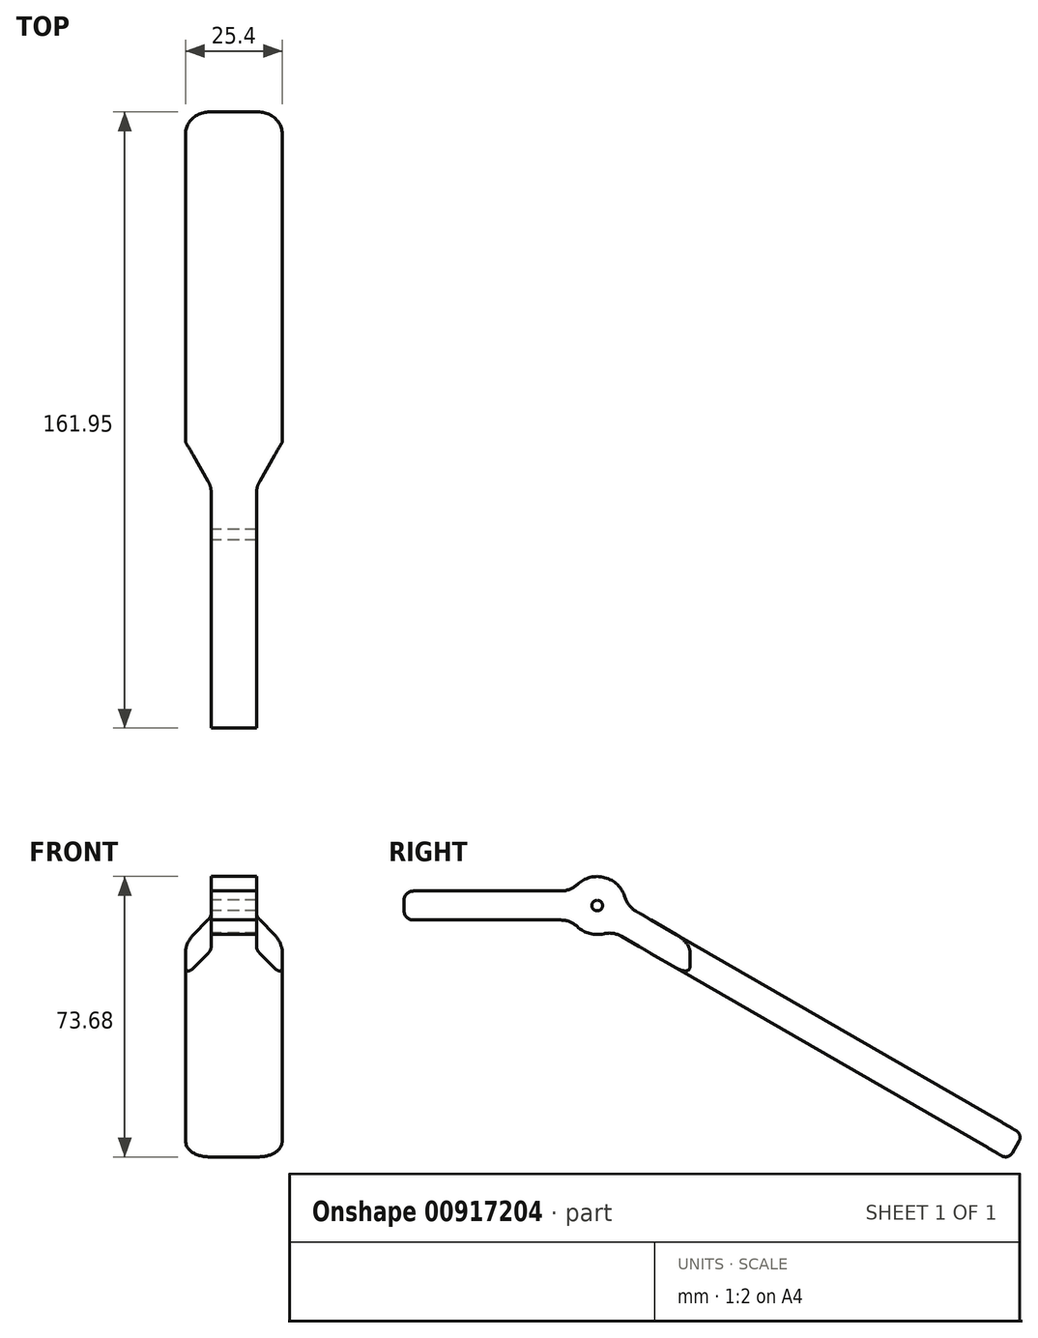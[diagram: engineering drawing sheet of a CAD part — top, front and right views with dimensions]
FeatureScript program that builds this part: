
annotation { "Feature Type Name" : "Feature", "Feature Type Description" : "" }
export const myFeature = defineFeature(function(context is Context, id is Id, definition is map)
    precondition{}
    {
        {
            var Q0;
            Q0=qCreatedBy(makeId("Right.planeOp"),FACE);
            var sketch = newSketch(context, id + "F0", { "sketchPlane" : qUnion([Q0])});
            skCircle(sketch, "E0", {"center": v(0, 0) * mm, "radius": 1.4 * mm});
            skLineSegment(sketch, "E1.bottom", {"start": v(-6.6, -3.81) * mm, "end": v(-50.8, -3.81) * mm});
            skLineSegment(sketch, "E1.top", {"start": v(-6.6, 3.81) * mm, "end": v(-50.8, 3.81) * mm});
            skLineSegment(sketch, "E1.right", {"start": v(-50.8, -3.81) * mm, "end": v(-50.8, 3.81) * mm});
            skPoint(sketch, "E1.middle", {"position": v(-28.7, 0) * mm});
            skLineSegment(sketch, "E2", {"start": v(3.81, -6.6) * mm, "end": v(108.08, -66.8) * mm});
            skLineSegment(sketch, "E3", {"start": v(108.08, -66.8) * mm, "end": v(111.9, -60.2) * mm});
            skLineSegment(sketch, "E4", {"start": v(111.9, -60.2) * mm, "end": v(7.62, 0) * mm});
            skLineSegment(sketch, "E5", {"start": v(0, 0) * mm, "end": v(33.46, -19.32) * mm, "construction": true});
            skLineSegment(sketch, "E6", {"start": v(-152.3, 12.7) * mm, "end": v(68.42, 12.7) * mm, "construction": true});
            skArc(sketch, "E7", {"start": v(-6.6, -3.8) * mm, "mid": v(-1.97, -7.36) * mm, "end": v(3.81, -6.6) * mm});
            skArc(sketch, "E8.trimOffspring", {"start": v(7.62, 0) * mm, "mid": v(1.97, 7.36) * mm, "end": v(-6.6, 3.8) * mm});
            skSolve(sketch);
        }
        {
            var Q0;
            Q0=qSketchRegion(id+"F0",true);
            extrude(context, id + "F1", {"entities" : qUnion([Q0]), "depth" : 25.4 * mm, "offsetDistance" : 25.4 * mm});
        }
        {
            var Q0;
            Q0=qCreatedBy(makeId("Top.planeOp"),FACE);
            cPlane(context, id + "F2", {"entities" : qUnion([Q0]), "cplaneType" : CPlaneType.OFFSET, "offset" : 25.4 * mm, "width" : 152.4 * mm, "height" : 152.4 * mm});
        }
        {
            var Q0;
            Q0=makeQuery(id+"F1.opExtrude","CAP_FACE",FACE,{"disambiguationData":[OSD([sQuery(id+"F0.wireOp",EDGE,"E0"),sQuery(id+"F0.wireOp",EDGE,"w8Ws021I-NBfv-kzaN-iq3K-uN73JVfCB56X"),sQuery(id+"F0.wireOp",EDGE,"E1.bottom"),sQuery(id+"F0.wireOp",EDGE,"E1.top"),sQuery(id+"F0.wireOp",EDGE,"E1.right"),sQuery(id+"F0.wireOp",EDGE,"E2"),sQuery(id+"F0.wireOp",EDGE,"E3"),sQuery(id+"F0.wireOp",EDGE,"E4"),sQuery(id+"F0.wireOp",EDGE,"a2025f1e-f919-408e-afa6-1f2dc75ffb8d.trimOffspring")])],"isStart":false});
            var Q1;
            Q1=makeQuery(id+"F1.opExtrude","CAP_FACE",FACE,{"disambiguationData":[OSD([sQuery(id+"F0.wireOp",EDGE,"E0"),sQuery(id+"F0.wireOp",EDGE,"w8Ws021I-NBfv-kzaN-iq3K-uN73JVfCB56X"),sQuery(id+"F0.wireOp",EDGE,"E1.bottom"),sQuery(id+"F0.wireOp",EDGE,"E1.top"),sQuery(id+"F0.wireOp",EDGE,"E1.right"),sQuery(id+"F0.wireOp",EDGE,"E2"),sQuery(id+"F0.wireOp",EDGE,"E3"),sQuery(id+"F0.wireOp",EDGE,"E4"),sQuery(id+"F0.wireOp",EDGE,"a2025f1e-f919-408e-afa6-1f2dc75ffb8d.trimOffspring")])],"isStart":true});
            cPlane(context, id + "F3", {"entities" : qUnion([Q0, Q1]), "cplaneType" : CPlaneType.MID_PLANE, "offset" : 25.4 * mm, "width" : 152.4 * mm, "height" : 152.4 * mm});
        }
        {
            var Q0;
            Q0=qCreatedBy(id+"F2.planeOp",FACE);
            var sketch = newSketch(context, id + "F4", { "sketchPlane" : qUnion([Q0])});
            skLineSegment(sketch, "E9.right", {"start": v(6.73, 12.7) * mm, "end": v(6.73, -50.8) * mm});
            skLineSegment(sketch, "E10.MirrorCS", {"start": v(18.67, 12.7) * mm, "end": v(18.67, -50.8) * mm});
            skLineSegment(sketch, "E11", {"start": v(6.73, 12.7) * mm, "end": v(0, 24.36) * mm});
            skLineSegment(sketch, "E12", {"start": v(0, 24.36) * mm, "end": v(0, -50.8) * mm});
            skLineSegment(sketch, "E13.MirrorCS", {"start": v(18.67, 12.7) * mm, "end": v(25.4, 24.36) * mm});
            skLineSegment(sketch, "E14.MirrorCS", {"start": v(25.4, 24.36) * mm, "end": v(25.4, -50.8) * mm});
            skLineSegment(sketch, "E15", {"start": v(0, -50.8) * mm, "end": v(6.73, -50.8) * mm});
            skLineSegment(sketch, "E16.MirrorCS", {"start": v(25.4, -50.8) * mm, "end": v(18.67, -50.8) * mm});
            skSolve(sketch);
        }
        {
            var Q0;
            Q0=makeQuery(id+"F4.imprint","IMPRINT",FACE,{"disambiguationData":[TD([[makeQuery(id+"F4.imprint","IMPRINT",EDGE,{"derivedFrom":sQuery(id+"F4.wireOp",EDGE,"E9.right")}),-1.0]])]});
            var Q1;
            Q1=makeQuery(id+"F4.imprint","IMPRINT",FACE,{"disambiguationData":[TD([[makeQuery(id+"F4.imprint","IMPRINT",EDGE,{"derivedFrom":sQuery(id+"F4.wireOp",EDGE,"E10.MirrorCS")}),1.0]])]});
            extrude(context, id + "F5", {"entities" : qUnion([Q0, Q1]), "operationType" : NewBodyOperationType.REMOVE, "endBound" : BoundingType.THROUGH_ALL, "oppositeDirection" : true, "depth" : 25.4 * mm, "offsetDistance" : 25.4 * mm});
        }
        {
            var Q0;
            Q0=makeQuery(id+"F1.opExtrude","SWEPT_EDGE",EDGE,{"disambiguationData":[OSD([sQuery(id+"F0.wireOp",EDGE,"E1.bottom"),sQuery(id+"F0.wireOp",EDGE,"E7")])]});
            var Q1;
            Q1=makeQuery(id+"F1.opExtrude","SWEPT_EDGE",EDGE,{"disambiguationData":[OSD([sQuery(id+"F0.wireOp",EDGE,"E2"),sQuery(id+"F0.wireOp",EDGE,"E7")])]});
            var Q2;
            Q2=makeQuery(id+"F1.opExtrude","SWEPT_EDGE",EDGE,{"disambiguationData":[OSD([sQuery(id+"F0.wireOp",EDGE,"E1.top"),sQuery(id+"F0.wireOp",EDGE,"E8.trimOffspring")])]});
            var Q3;
            Q3=makeQuery(id+"F1.opExtrude","SWEPT_EDGE",EDGE,{"disambiguationData":[OSD([sQuery(id+"F0.wireOp",EDGE,"E4"),sQuery(id+"F0.wireOp",EDGE,"E8.trimOffspring")])]});
            var Q4;
            Q4=makeQuery(id+"F5.boolean.opBoolean","COPY",EDGE,{"derivedFrom":makeQuery(id+"F5.opExtrude","SWEPT_EDGE",EDGE,{"disambiguationData":[OSD([sQuery(id+"F4.wireOp",EDGE,"E10.MirrorCS"),sQuery(id+"F4.wireOp",EDGE,"E13.MirrorCS")])]})});
            var Q5;
            Q5=makeQuery(id+"F5.boolean.opBoolean","COPY",EDGE,{"derivedFrom":makeQuery(id+"F5.opExtrude","SWEPT_EDGE",EDGE,{"disambiguationData":[OSD([sQuery(id+"F4.wireOp",EDGE,"E13.MirrorCS"),sQuery(id+"F4.wireOp",EDGE,"E14.MirrorCS")])]})});
            var Q6;
            Q6=makeQuery(id+"F5.boolean.opBoolean","COPY",EDGE,{"derivedFrom":makeQuery(id+"F5.opExtrude","SWEPT_EDGE",EDGE,{"disambiguationData":[OSD([sQuery(id+"F4.wireOp",EDGE,"E9.right"),sQuery(id+"F4.wireOp",EDGE,"E11")])]})});
            var Q7;
            Q7=makeQuery(id+"F5.boolean.opBoolean","COPY",EDGE,{"derivedFrom":makeQuery(id+"F5.opExtrude","SWEPT_EDGE",EDGE,{"disambiguationData":[OSD([sQuery(id+"F4.wireOp",EDGE,"E11"),sQuery(id+"F4.wireOp",EDGE,"E12")])]})});
            var Q8;
            Q8=makeQuery(id+"F1.opExtrude","CAP_EDGE",EDGE,{"disambiguationData":[OSD([sQuery(id+"F0.wireOp",EDGE,"E3")])],"isStart":true});
            var Q9;
            Q9=makeQuery(id+"F1.opExtrude","CAP_EDGE",EDGE,{"disambiguationData":[OSD([sQuery(id+"F0.wireOp",EDGE,"E3")])],"isStart":false});
            fillet(context, id + "F6", {"entities" : qUnion([Q0, Q1, Q2, Q3, Q4, Q5, Q6, Q7, Q8, Q9]), "radius" : 6.35 * mm, "tangentPropagation" : true, "allowEdgeOverflow" : false});
        }
        {
            var Q0;
            Q0=makeQuery(id+"F1.opExtrude","SWEPT_EDGE",EDGE,{"disambiguationData":[OSD([sQuery(id+"F0.wireOp",EDGE,"E1.bottom"),sQuery(id+"F0.wireOp",EDGE,"E1.right")])]});
            var Q1;
            Q1=makeQuery(id+"F1.opExtrude","SWEPT_EDGE",EDGE,{"disambiguationData":[OSD([sQuery(id+"F0.wireOp",EDGE,"E1.top"),sQuery(id+"F0.wireOp",EDGE,"E1.right")])]});
            fillet(context, id + "F7", {"entities" : qUnion([Q0, Q1]), "radius" : 2.54 * mm, "tangentPropagation" : true, "allowEdgeOverflow" : false});
        }
        {
            var Q0;
            {var subQ0=sQuery(id+"F0.wireOp",EDGE,"E2");var subQ1=sQuery(id+"F0.wireOp",EDGE,"w8Ws021I-NBfv-kzaN-iq3K-uN73JVfCB56X");Q0=makeQuery(id+"F6.opFillet","BLEND_EDGE",EDGE,{"blendedFrom":[makeQuery(id+"F1.opExtrude","SWEPT_EDGE",EDGE,{"disambiguationData":[OSD([subQ1,subQ0])]}),makeQuery(id+"F1.opExtrude","CAP_FACE",FACE,{"disambiguationData":[OSD([sQuery(id+"F0.wireOp",EDGE,"E0"),subQ1,sQuery(id+"F0.wireOp",EDGE,"E1.bottom"),sQuery(id+"F0.wireOp",EDGE,"E1.top"),sQuery(id+"F0.wireOp",EDGE,"E1.right"),subQ0,sQuery(id+"F0.wireOp",EDGE,"E3"),sQuery(id+"F0.wireOp",EDGE,"E4"),sQuery(id+"F0.wireOp",EDGE,"a2025f1e-f919-408e-afa6-1f2dc75ffb8d.trimOffspring")])],"isStart":false})],"blendedInto":[makeQuery(id+"F1.opExtrude","CAP_FACE",FACE,{"disambiguationData":[OSD([sQuery(id+"F0.wireOp",EDGE,"E0"),subQ1,sQuery(id+"F0.wireOp",EDGE,"E1.bottom"),sQuery(id+"F0.wireOp",EDGE,"E1.top"),sQuery(id+"F0.wireOp",EDGE,"E1.right"),subQ0,sQuery(id+"F0.wireOp",EDGE,"E3"),sQuery(id+"F0.wireOp",EDGE,"E4"),sQuery(id+"F0.wireOp",EDGE,"a2025f1e-f919-408e-afa6-1f2dc75ffb8d.trimOffspring")])],"isStart":false})]});}
            var Q1;
            Q1=makeQuery(id+"F1.opExtrude","CAP_EDGE",EDGE,{"disambiguationData":[OSD([sQuery(id+"F0.wireOp",EDGE,"E1.bottom")])],"isStart":false});
            var Q2;
            Q2=makeQuery(id+"F1.opExtrude","CAP_EDGE",EDGE,{"disambiguationData":[OSD([sQuery(id+"F0.wireOp",EDGE,"E2")])],"isStart":false});
            var Q3;
            Q3=makeQuery(id+"F1.opExtrude","SWEPT_EDGE",EDGE,{"disambiguationData":[OSD([sQuery(id+"F0.wireOp",EDGE,"E1.top"),sQuery(id+"F0.wireOp",EDGE,"E1.right")])]});
            var Q4;
            Q4=makeQuery(id+"F1.opExtrude","SWEPT_EDGE",EDGE,{"disambiguationData":[OSD([sQuery(id+"F0.wireOp",EDGE,"E2"),sQuery(id+"F0.wireOp",EDGE,"E3")])]});
            var Q5;
            Q5=makeQuery(id+"F1.opExtrude","CAP_EDGE",EDGE,{"disambiguationData":[OSD([sQuery(id+"F0.wireOp",EDGE,"E4")])],"isStart":false});
            var Q6;
            Q6=makeQuery(id+"F1.opExtrude","CAP_EDGE",EDGE,{"disambiguationData":[OSD([sQuery(id+"F0.wireOp",EDGE,"E1.top")])],"isStart":false});
            var Q7;
            Q7=makeQuery(id+"F1.opExtrude","CAP_EDGE",EDGE,{"disambiguationData":[OSD([sQuery(id+"F0.wireOp",EDGE,"a2025f1e-f919-408e-afa6-1f2dc75ffb8d.trimOffspring")])],"isStart":false});
            var Q8;
            {var subQ0=sQuery(id+"F0.wireOp",EDGE,"a2025f1e-f919-408e-afa6-1f2dc75ffb8d.trimOffspring");var subQ1=sQuery(id+"F0.wireOp",EDGE,"E4");Q8=makeQuery(id+"F6.opFillet","BLEND_EDGE",EDGE,{"blendedFrom":[makeQuery(id+"F1.opExtrude","SWEPT_EDGE",EDGE,{"disambiguationData":[OSD([subQ1,subQ0])]}),makeQuery(id+"F1.opExtrude","CAP_FACE",FACE,{"disambiguationData":[OSD([sQuery(id+"F0.wireOp",EDGE,"E0"),sQuery(id+"F0.wireOp",EDGE,"w8Ws021I-NBfv-kzaN-iq3K-uN73JVfCB56X"),sQuery(id+"F0.wireOp",EDGE,"E1.bottom"),sQuery(id+"F0.wireOp",EDGE,"E1.top"),sQuery(id+"F0.wireOp",EDGE,"E1.right"),sQuery(id+"F0.wireOp",EDGE,"E2"),sQuery(id+"F0.wireOp",EDGE,"E3"),subQ1,subQ0])],"isStart":false})],"blendedInto":[makeQuery(id+"F1.opExtrude","CAP_FACE",FACE,{"disambiguationData":[OSD([sQuery(id+"F0.wireOp",EDGE,"E0"),sQuery(id+"F0.wireOp",EDGE,"w8Ws021I-NBfv-kzaN-iq3K-uN73JVfCB56X"),sQuery(id+"F0.wireOp",EDGE,"E1.bottom"),sQuery(id+"F0.wireOp",EDGE,"E1.top"),sQuery(id+"F0.wireOp",EDGE,"E1.right"),sQuery(id+"F0.wireOp",EDGE,"E2"),sQuery(id+"F0.wireOp",EDGE,"E3"),subQ1,subQ0])],"isStart":false})]});}
            var Q9;
            Q9=makeQuery(id+"F1.opExtrude","CAP_EDGE",EDGE,{"disambiguationData":[OSD([sQuery(id+"F0.wireOp",EDGE,"E1.bottom")])],"isStart":true});
            var Q10;
            Q10=makeQuery(id+"F1.opExtrude","SWEPT_EDGE",EDGE,{"disambiguationData":[OSD([sQuery(id+"F0.wireOp",EDGE,"E1.bottom"),sQuery(id+"F0.wireOp",EDGE,"E1.right")])]});
            var Q11;
            Q11=makeQuery(id+"F1.opExtrude","CAP_EDGE",EDGE,{"disambiguationData":[OSD([sQuery(id+"F0.wireOp",EDGE,"w8Ws021I-NBfv-kzaN-iq3K-uN73JVfCB56X")])],"isStart":false});
            var Q12;
            Q12=makeQuery(id+"F1.opExtrude","CAP_EDGE",EDGE,{"disambiguationData":[OSD([sQuery(id+"F0.wireOp",EDGE,"E3")])],"isStart":true});
            var Q13;
            Q13=makeQuery(id+"F1.opExtrude","CAP_EDGE",EDGE,{"disambiguationData":[OSD([sQuery(id+"F0.wireOp",EDGE,"E1.right")])],"isStart":false});
            var Q14;
            {var subQ0=sQuery(id+"F0.wireOp",EDGE,"a2025f1e-f919-408e-afa6-1f2dc75ffb8d.trimOffspring");var subQ1=sQuery(id+"F0.wireOp",EDGE,"E1.top");Q14=makeQuery(id+"F6.opFillet","BLEND_EDGE",EDGE,{"blendedFrom":[makeQuery(id+"F1.opExtrude","SWEPT_EDGE",EDGE,{"disambiguationData":[OSD([subQ1,subQ0])]}),makeQuery(id+"F1.opExtrude","CAP_FACE",FACE,{"disambiguationData":[OSD([sQuery(id+"F0.wireOp",EDGE,"E0"),sQuery(id+"F0.wireOp",EDGE,"w8Ws021I-NBfv-kzaN-iq3K-uN73JVfCB56X"),sQuery(id+"F0.wireOp",EDGE,"E1.bottom"),subQ1,sQuery(id+"F0.wireOp",EDGE,"E1.right"),sQuery(id+"F0.wireOp",EDGE,"E2"),sQuery(id+"F0.wireOp",EDGE,"E3"),sQuery(id+"F0.wireOp",EDGE,"E4"),subQ0])],"isStart":false})],"blendedInto":[makeQuery(id+"F1.opExtrude","CAP_FACE",FACE,{"disambiguationData":[OSD([sQuery(id+"F0.wireOp",EDGE,"E0"),sQuery(id+"F0.wireOp",EDGE,"w8Ws021I-NBfv-kzaN-iq3K-uN73JVfCB56X"),sQuery(id+"F0.wireOp",EDGE,"E1.bottom"),subQ1,sQuery(id+"F0.wireOp",EDGE,"E1.right"),sQuery(id+"F0.wireOp",EDGE,"E2"),sQuery(id+"F0.wireOp",EDGE,"E3"),sQuery(id+"F0.wireOp",EDGE,"E4"),subQ0])],"isStart":false})]});}
            var Q15;
            Q15=makeQuery(id+"F1.opExtrude","CAP_EDGE",EDGE,{"disambiguationData":[OSD([sQuery(id+"F0.wireOp",EDGE,"w8Ws021I-NBfv-kzaN-iq3K-uN73JVfCB56X")])],"isStart":true});
            var Q16;
            {var subQ0=sQuery(id+"F0.wireOp",EDGE,"E1.bottom");var subQ1=sQuery(id+"F0.wireOp",EDGE,"w8Ws021I-NBfv-kzaN-iq3K-uN73JVfCB56X");Q16=makeQuery(id+"F6.opFillet","BLEND_EDGE",EDGE,{"blendedFrom":[makeQuery(id+"F1.opExtrude","SWEPT_EDGE",EDGE,{"disambiguationData":[OSD([subQ1,subQ0])]}),makeQuery(id+"F1.opExtrude","CAP_FACE",FACE,{"disambiguationData":[OSD([sQuery(id+"F0.wireOp",EDGE,"E0"),subQ1,subQ0,sQuery(id+"F0.wireOp",EDGE,"E1.top"),sQuery(id+"F0.wireOp",EDGE,"E1.right"),sQuery(id+"F0.wireOp",EDGE,"E2"),sQuery(id+"F0.wireOp",EDGE,"E3"),sQuery(id+"F0.wireOp",EDGE,"E4"),sQuery(id+"F0.wireOp",EDGE,"a2025f1e-f919-408e-afa6-1f2dc75ffb8d.trimOffspring")])],"isStart":true})],"blendedInto":[makeQuery(id+"F1.opExtrude","CAP_FACE",FACE,{"disambiguationData":[OSD([sQuery(id+"F0.wireOp",EDGE,"E0"),subQ1,subQ0,sQuery(id+"F0.wireOp",EDGE,"E1.top"),sQuery(id+"F0.wireOp",EDGE,"E1.right"),sQuery(id+"F0.wireOp",EDGE,"E2"),sQuery(id+"F0.wireOp",EDGE,"E3"),sQuery(id+"F0.wireOp",EDGE,"E4"),sQuery(id+"F0.wireOp",EDGE,"a2025f1e-f919-408e-afa6-1f2dc75ffb8d.trimOffspring")])],"isStart":true})]});}
            var Q17;
            {var subQ0=sQuery(id+"F0.wireOp",EDGE,"a2025f1e-f919-408e-afa6-1f2dc75ffb8d.trimOffspring");var subQ1=sQuery(id+"F0.wireOp",EDGE,"E1.top");Q17=makeQuery(id+"F6.opFillet","BLEND_EDGE",EDGE,{"blendedFrom":[makeQuery(id+"F1.opExtrude","SWEPT_EDGE",EDGE,{"disambiguationData":[OSD([subQ1,subQ0])]}),makeQuery(id+"F1.opExtrude","CAP_FACE",FACE,{"disambiguationData":[OSD([sQuery(id+"F0.wireOp",EDGE,"E0"),sQuery(id+"F0.wireOp",EDGE,"w8Ws021I-NBfv-kzaN-iq3K-uN73JVfCB56X"),sQuery(id+"F0.wireOp",EDGE,"E1.bottom"),subQ1,sQuery(id+"F0.wireOp",EDGE,"E1.right"),sQuery(id+"F0.wireOp",EDGE,"E2"),sQuery(id+"F0.wireOp",EDGE,"E3"),sQuery(id+"F0.wireOp",EDGE,"E4"),subQ0])],"isStart":true})],"blendedInto":[makeQuery(id+"F1.opExtrude","CAP_FACE",FACE,{"disambiguationData":[OSD([sQuery(id+"F0.wireOp",EDGE,"E0"),sQuery(id+"F0.wireOp",EDGE,"w8Ws021I-NBfv-kzaN-iq3K-uN73JVfCB56X"),sQuery(id+"F0.wireOp",EDGE,"E1.bottom"),subQ1,sQuery(id+"F0.wireOp",EDGE,"E1.right"),sQuery(id+"F0.wireOp",EDGE,"E2"),sQuery(id+"F0.wireOp",EDGE,"E3"),sQuery(id+"F0.wireOp",EDGE,"E4"),subQ0])],"isStart":true})]});}
            var Q18;
            Q18=makeQuery(id+"F1.opExtrude","SWEPT_EDGE",EDGE,{"disambiguationData":[OSD([sQuery(id+"F0.wireOp",EDGE,"E3"),sQuery(id+"F0.wireOp",EDGE,"E4")])]});
            var Q19;
            {var subQ0=sQuery(id+"F0.wireOp",EDGE,"a2025f1e-f919-408e-afa6-1f2dc75ffb8d.trimOffspring");Q19=makeQuery(id+"F6.opFillet","BLEND_EDGE",EDGE,{"blendedFrom":[makeQuery(id+"F1.opExtrude","SWEPT_EDGE",EDGE,{"disambiguationData":[OSD([sQuery(id+"F0.wireOp",EDGE,"E4"),subQ0])]}),makeQuery(id+"F1.opExtrude","SWEPT_FACE",FACE,{"disambiguationData":[OSD([subQ0])]})],"blendedInto":[makeQuery(id+"F1.opExtrude","SWEPT_FACE",FACE,{"disambiguationData":[OSD([subQ0])]})]});}
            var Q20;
            {var subQ0=sQuery(id+"F0.wireOp",EDGE,"w8Ws021I-NBfv-kzaN-iq3K-uN73JVfCB56X");Q20=makeQuery(id+"F6.opFillet","BLEND_EDGE",EDGE,{"blendedFrom":[makeQuery(id+"F1.opExtrude","SWEPT_EDGE",EDGE,{"disambiguationData":[OSD([subQ0,sQuery(id+"F0.wireOp",EDGE,"E1.bottom")])]}),makeQuery(id+"F1.opExtrude","SWEPT_FACE",FACE,{"disambiguationData":[OSD([subQ0])]})],"blendedInto":[makeQuery(id+"F1.opExtrude","SWEPT_FACE",FACE,{"disambiguationData":[OSD([subQ0])]})]});}
            var Q21;
            {var subQ0=sQuery(id+"F0.wireOp",EDGE,"E1.top");Q21=makeQuery(id+"F6.opFillet","BLEND_EDGE",EDGE,{"blendedFrom":[makeQuery(id+"F1.opExtrude","SWEPT_EDGE",EDGE,{"disambiguationData":[OSD([subQ0,sQuery(id+"F0.wireOp",EDGE,"a2025f1e-f919-408e-afa6-1f2dc75ffb8d.trimOffspring")])]}),makeQuery(id+"F1.opExtrude","SWEPT_FACE",FACE,{"disambiguationData":[OSD([subQ0])]})],"blendedInto":[makeQuery(id+"F1.opExtrude","SWEPT_FACE",FACE,{"disambiguationData":[OSD([subQ0])]})]});}
            var Q22;
            {var subQ0=sQuery(id+"F0.wireOp",EDGE,"a2025f1e-f919-408e-afa6-1f2dc75ffb8d.trimOffspring");var subQ1=sQuery(id+"F0.wireOp",EDGE,"E4");Q22=makeQuery(id+"F6.opFillet","BLEND_EDGE",EDGE,{"blendedFrom":[makeQuery(id+"F1.opExtrude","SWEPT_EDGE",EDGE,{"disambiguationData":[OSD([subQ1,subQ0])]}),makeQuery(id+"F1.opExtrude","CAP_FACE",FACE,{"disambiguationData":[OSD([sQuery(id+"F0.wireOp",EDGE,"E0"),sQuery(id+"F0.wireOp",EDGE,"w8Ws021I-NBfv-kzaN-iq3K-uN73JVfCB56X"),sQuery(id+"F0.wireOp",EDGE,"E1.bottom"),sQuery(id+"F0.wireOp",EDGE,"E1.top"),sQuery(id+"F0.wireOp",EDGE,"E1.right"),sQuery(id+"F0.wireOp",EDGE,"E2"),sQuery(id+"F0.wireOp",EDGE,"E3"),subQ1,subQ0])],"isStart":true})],"blendedInto":[makeQuery(id+"F1.opExtrude","CAP_FACE",FACE,{"disambiguationData":[OSD([sQuery(id+"F0.wireOp",EDGE,"E0"),sQuery(id+"F0.wireOp",EDGE,"w8Ws021I-NBfv-kzaN-iq3K-uN73JVfCB56X"),sQuery(id+"F0.wireOp",EDGE,"E1.bottom"),sQuery(id+"F0.wireOp",EDGE,"E1.top"),sQuery(id+"F0.wireOp",EDGE,"E1.right"),sQuery(id+"F0.wireOp",EDGE,"E2"),sQuery(id+"F0.wireOp",EDGE,"E3"),subQ1,subQ0])],"isStart":true})]});}
            var Q23;
            {var subQ0=sQuery(id+"F0.wireOp",EDGE,"E1.bottom");Q23=makeQuery(id+"F6.opFillet","BLEND_EDGE",EDGE,{"blendedFrom":[makeQuery(id+"F1.opExtrude","SWEPT_EDGE",EDGE,{"disambiguationData":[OSD([sQuery(id+"F0.wireOp",EDGE,"w8Ws021I-NBfv-kzaN-iq3K-uN73JVfCB56X"),subQ0])]}),makeQuery(id+"F1.opExtrude","SWEPT_FACE",FACE,{"disambiguationData":[OSD([subQ0])]})],"blendedInto":[makeQuery(id+"F1.opExtrude","SWEPT_FACE",FACE,{"disambiguationData":[OSD([subQ0])]})]});}
            var Q24;
            Q24=makeQuery(id+"F1.opExtrude","CAP_EDGE",EDGE,{"disambiguationData":[OSD([sQuery(id+"F0.wireOp",EDGE,"E1.right")])],"isStart":true});
            var Q25;
            Q25=makeQuery(id+"F1.opExtrude","CAP_EDGE",EDGE,{"disambiguationData":[OSD([sQuery(id+"F0.wireOp",EDGE,"E2")])],"isStart":true});
            var Q26;
            {var subQ0=sQuery(id+"F0.wireOp",EDGE,"a2025f1e-f919-408e-afa6-1f2dc75ffb8d.trimOffspring");Q26=makeQuery(id+"F6.opFillet","BLEND_EDGE",EDGE,{"blendedFrom":[makeQuery(id+"F1.opExtrude","SWEPT_EDGE",EDGE,{"disambiguationData":[OSD([sQuery(id+"F0.wireOp",EDGE,"E1.top"),subQ0])]}),makeQuery(id+"F1.opExtrude","SWEPT_FACE",FACE,{"disambiguationData":[OSD([subQ0])]})],"blendedInto":[makeQuery(id+"F1.opExtrude","SWEPT_FACE",FACE,{"disambiguationData":[OSD([subQ0])]})]});}
            var Q27;
            Q27=makeQuery(id+"F1.opExtrude","CAP_EDGE",EDGE,{"disambiguationData":[OSD([sQuery(id+"F0.wireOp",EDGE,"E3")])],"isStart":false});
            var Q28;
            Q28=makeQuery(id+"F1.opExtrude","CAP_EDGE",EDGE,{"disambiguationData":[OSD([sQuery(id+"F0.wireOp",EDGE,"a2025f1e-f919-408e-afa6-1f2dc75ffb8d.trimOffspring")])],"isStart":true});
            var Q29;
            {var subQ0=sQuery(id+"F0.wireOp",EDGE,"E2");Q29=makeQuery(id+"F6.opFillet","BLEND_EDGE",EDGE,{"blendedFrom":[makeQuery(id+"F1.opExtrude","SWEPT_EDGE",EDGE,{"disambiguationData":[OSD([sQuery(id+"F0.wireOp",EDGE,"w8Ws021I-NBfv-kzaN-iq3K-uN73JVfCB56X"),subQ0])]}),makeQuery(id+"F1.opExtrude","SWEPT_FACE",FACE,{"disambiguationData":[OSD([subQ0])]})],"blendedInto":[makeQuery(id+"F1.opExtrude","SWEPT_FACE",FACE,{"disambiguationData":[OSD([subQ0])]})]});}
            var Q30;
            {var subQ0=sQuery(id+"F0.wireOp",EDGE,"w8Ws021I-NBfv-kzaN-iq3K-uN73JVfCB56X");Q30=makeQuery(id+"F6.opFillet","BLEND_EDGE",EDGE,{"blendedFrom":[makeQuery(id+"F1.opExtrude","SWEPT_EDGE",EDGE,{"disambiguationData":[OSD([subQ0,sQuery(id+"F0.wireOp",EDGE,"E2")])]}),makeQuery(id+"F1.opExtrude","SWEPT_FACE",FACE,{"disambiguationData":[OSD([subQ0])]})],"blendedInto":[makeQuery(id+"F1.opExtrude","SWEPT_FACE",FACE,{"disambiguationData":[OSD([subQ0])]})]});}
            var Q31;
            Q31=makeQuery(id+"F1.opExtrude","CAP_EDGE",EDGE,{"disambiguationData":[OSD([sQuery(id+"F0.wireOp",EDGE,"E1.top")])],"isStart":true});
            var Q32;
            {var subQ0=sQuery(id+"F0.wireOp",EDGE,"E4");Q32=makeQuery(id+"F6.opFillet","BLEND_EDGE",EDGE,{"blendedFrom":[makeQuery(id+"F1.opExtrude","SWEPT_EDGE",EDGE,{"disambiguationData":[OSD([subQ0,sQuery(id+"F0.wireOp",EDGE,"a2025f1e-f919-408e-afa6-1f2dc75ffb8d.trimOffspring")])]}),makeQuery(id+"F1.opExtrude","SWEPT_FACE",FACE,{"disambiguationData":[OSD([subQ0])]})],"blendedInto":[makeQuery(id+"F1.opExtrude","SWEPT_FACE",FACE,{"disambiguationData":[OSD([subQ0])]})]});}
            var Q33;
            Q33=makeQuery(id+"F1.opExtrude","CAP_EDGE",EDGE,{"disambiguationData":[OSD([sQuery(id+"F0.wireOp",EDGE,"E4")])],"isStart":true});
            var Q34;
            {var subQ0=sQuery(id+"F0.wireOp",EDGE,"E1.bottom");var subQ1=sQuery(id+"F0.wireOp",EDGE,"w8Ws021I-NBfv-kzaN-iq3K-uN73JVfCB56X");Q34=makeQuery(id+"F6.opFillet","BLEND_EDGE",EDGE,{"blendedFrom":[makeQuery(id+"F1.opExtrude","SWEPT_EDGE",EDGE,{"disambiguationData":[OSD([subQ1,subQ0])]}),makeQuery(id+"F1.opExtrude","CAP_FACE",FACE,{"disambiguationData":[OSD([sQuery(id+"F0.wireOp",EDGE,"E0"),subQ1,subQ0,sQuery(id+"F0.wireOp",EDGE,"E1.top"),sQuery(id+"F0.wireOp",EDGE,"E1.right"),sQuery(id+"F0.wireOp",EDGE,"E2"),sQuery(id+"F0.wireOp",EDGE,"E3"),sQuery(id+"F0.wireOp",EDGE,"E4"),sQuery(id+"F0.wireOp",EDGE,"a2025f1e-f919-408e-afa6-1f2dc75ffb8d.trimOffspring")])],"isStart":false})],"blendedInto":[makeQuery(id+"F1.opExtrude","CAP_FACE",FACE,{"disambiguationData":[OSD([sQuery(id+"F0.wireOp",EDGE,"E0"),subQ1,subQ0,sQuery(id+"F0.wireOp",EDGE,"E1.top"),sQuery(id+"F0.wireOp",EDGE,"E1.right"),sQuery(id+"F0.wireOp",EDGE,"E2"),sQuery(id+"F0.wireOp",EDGE,"E3"),sQuery(id+"F0.wireOp",EDGE,"E4"),sQuery(id+"F0.wireOp",EDGE,"a2025f1e-f919-408e-afa6-1f2dc75ffb8d.trimOffspring")])],"isStart":false})]});}
            var Q35;
            {var subQ0=sQuery(id+"F0.wireOp",EDGE,"E2");var subQ1=sQuery(id+"F0.wireOp",EDGE,"w8Ws021I-NBfv-kzaN-iq3K-uN73JVfCB56X");Q35=makeQuery(id+"F6.opFillet","BLEND_EDGE",EDGE,{"blendedFrom":[makeQuery(id+"F1.opExtrude","SWEPT_EDGE",EDGE,{"disambiguationData":[OSD([subQ1,subQ0])]}),makeQuery(id+"F1.opExtrude","CAP_FACE",FACE,{"disambiguationData":[OSD([sQuery(id+"F0.wireOp",EDGE,"E0"),subQ1,sQuery(id+"F0.wireOp",EDGE,"E1.bottom"),sQuery(id+"F0.wireOp",EDGE,"E1.top"),sQuery(id+"F0.wireOp",EDGE,"E1.right"),subQ0,sQuery(id+"F0.wireOp",EDGE,"E3"),sQuery(id+"F0.wireOp",EDGE,"E4"),sQuery(id+"F0.wireOp",EDGE,"a2025f1e-f919-408e-afa6-1f2dc75ffb8d.trimOffspring")])],"isStart":true})],"blendedInto":[makeQuery(id+"F1.opExtrude","CAP_FACE",FACE,{"disambiguationData":[OSD([sQuery(id+"F0.wireOp",EDGE,"E0"),subQ1,sQuery(id+"F0.wireOp",EDGE,"E1.bottom"),sQuery(id+"F0.wireOp",EDGE,"E1.top"),sQuery(id+"F0.wireOp",EDGE,"E1.right"),subQ0,sQuery(id+"F0.wireOp",EDGE,"E3"),sQuery(id+"F0.wireOp",EDGE,"E4"),sQuery(id+"F0.wireOp",EDGE,"a2025f1e-f919-408e-afa6-1f2dc75ffb8d.trimOffspring")])],"isStart":true})]});}
            fillet(context, id + "F8", {"entities" : qUnion([Q0, Q1, Q2, Q3, Q4, Q5, Q6, Q7, Q8, Q9, Q10, Q11, Q12, Q13, Q14, Q15, Q16, Q17, Q18, Q19, Q20, Q21, Q22, Q23, Q24, Q25, Q26, Q27, Q28, Q29, Q30, Q31, Q32, Q33, Q34, Q35]), "radius" : 2.03 * mm, "tangentPropagation" : true, "allowEdgeOverflow" : false});
        }
    });
